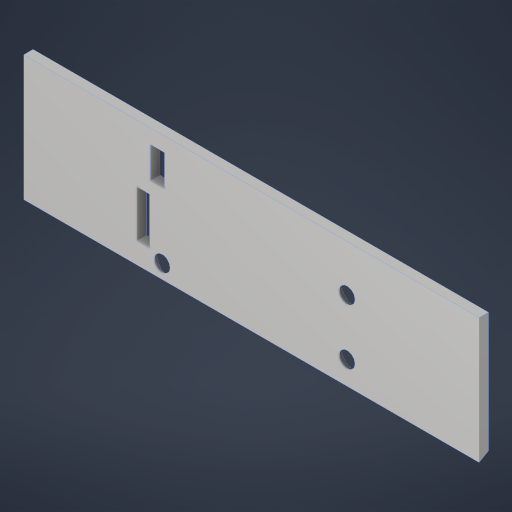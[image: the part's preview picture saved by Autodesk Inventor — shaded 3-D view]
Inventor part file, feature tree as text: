
AUTODESK INVENTOR PART (.ipt)
format: ipt  version: 2023 (Build 270158000, 158)  size: 212,992 bytes
history: native  units: mm
features: other x8, reference x7, sketch x4, extrude x3, hole x1
ambient origin geometry x8: Origin, YZ Plane, XZ Plane, XY Plane, X Axis, Y Axis, Z Axis, Center Point
bodies: Body1 (feature_tree)
feature tree (23):
  other  "Bryła1"
  extrude  "Wyciągnięcie proste1"  Depth=10.0mm TaperAngle=0.0deg
  hole  "Otwór1"  [1 undecoded]
  extrude  "Wyciągnięcie proste2"  Depth=10.0mm
  extrude  "Extrusion3"  Depth=10.0mm
  sketch  "Szkic1"
  sketch  "Szkic2"
  sketch  "Szkic3"
  reference  "Odniesienie1"
  reference  "Reference2"
  reference  "Reference3"
  reference  "Reference4"
  reference  "Reference5"
  reference  "Reference6"
  reference  "Reference7"
  sketch  "Sketch4"  dims[d1=2.0mm d2=98.0mm d3=0.0mm d8=3.4mm d9=5.3mm d10=6.9mm d11=2.0mm d12=14.7mm d13=5.5mm d14=20.594885mm d17=5.2mm d18=4.55mm d19=2.7mm d20=10.0mm d21=2.0mm d22=17.2mm d23=6.7mm d24=3.0mm d25=10.0mm d26=0.0mm d27=2.0mm d31=30.0deg d32=0.0mm d33=0.0mm]
  parser-record x1  (decoder bookkeeping rows leaked as tree rows — omitted from the tree; the rows remain in map.json)
  other  "Zlozenie.iam"
  other  "PrzekladniaPrawa:1"
  other  "MocowaniePrawejPrzekladni:1"
  other  "PrzekladniaLewa:1"
  other  "MocowanieLewejPrzekladni:1"
  other  "Blacha:1"
note: 1 required parameter value undecoded (feature->parameter linkage not recoverable at this tier; creation-order binding heuristic only, values carry confidence <= 0.55)
note: 1 file-system path scrubbed to <path> (originals preserved in map.json)
